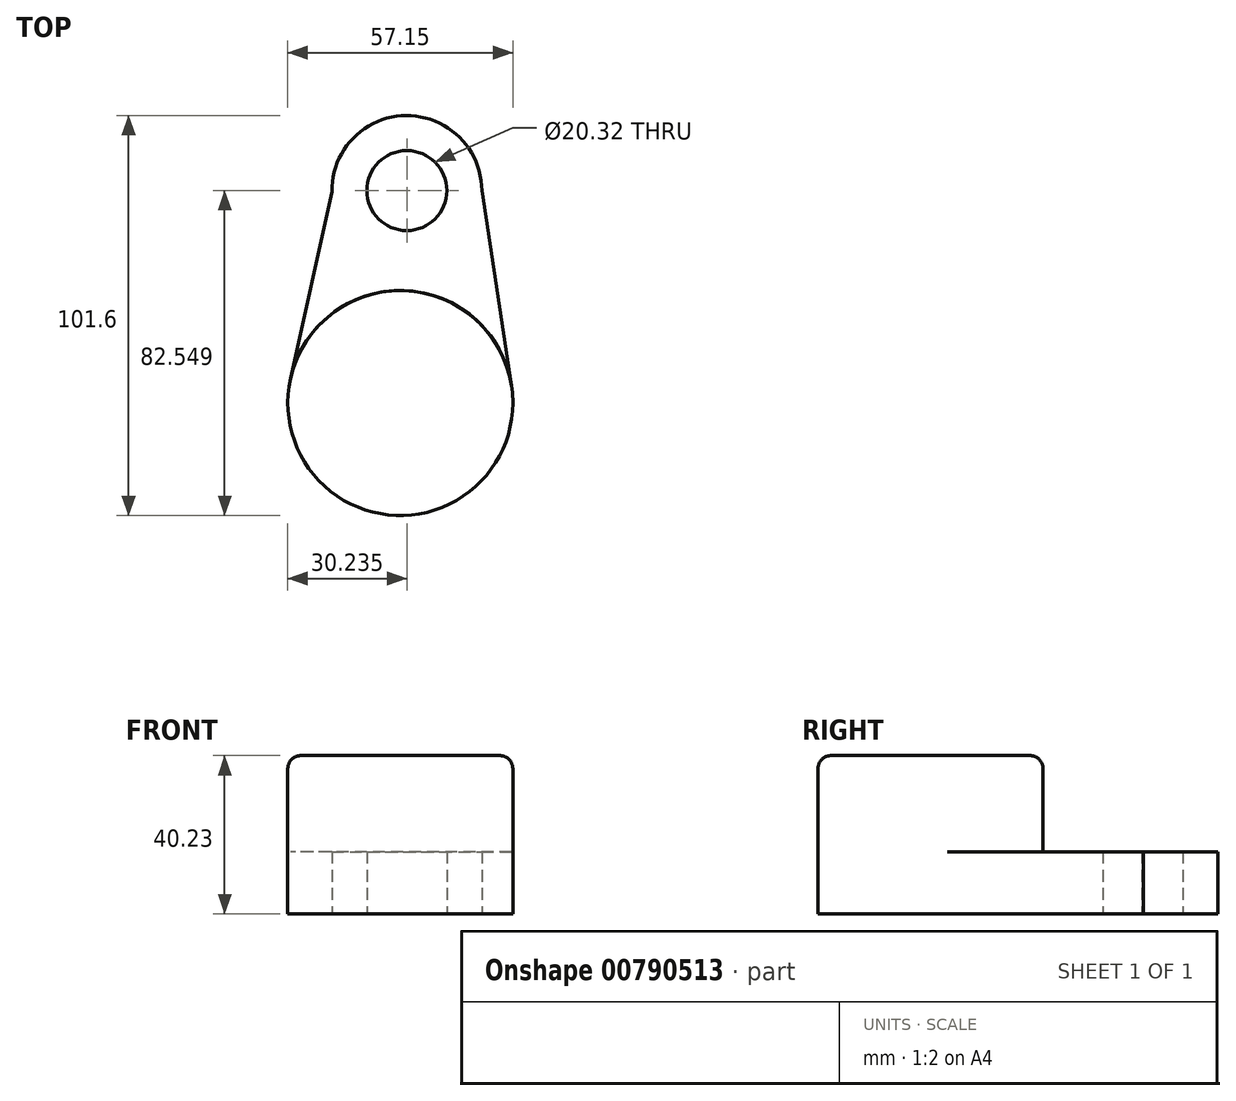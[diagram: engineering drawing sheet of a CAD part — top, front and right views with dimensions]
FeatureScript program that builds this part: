
annotation { "Feature Type Name" : "Feature", "Feature Type Description" : "" }
export const myFeature = defineFeature(function(context is Context, id is Id, definition is map)
    precondition{}
    {
        {
            var Q0;
            Q0=qCreatedBy(makeId("Top.planeOp"),FACE);
            var sketch = newSketch(context, id + "F0", { "sketchPlane" : qUnion([Q0])});
            skCircle(sketch, "E0", {"center": v(-37.45, -20.99) * mm, "radius": 28.58 * mm});
            skSolve(sketch);
        }
        {
            var Q0;
            Q0 = qSketchRegion(id + "F0", true);
            extrude(context, id + "F1", {"entities" : qUnion([Q0]), "depth" : 40.23 * mm, "offsetDistance" : 25.4 * mm});
        }
        {
            var Q0;
            Q0=makeQuery(id+"F1.opExtrude","CAP_FACE",FACE,{"disambiguationData":[OSD([sQuery(id+"F0.wireOp",EDGE,"E0")])],"isStart":false});
            fillet(context, id + "F2", {"entities" : qUnion([Q0]), "radius" : 3.3 * mm, "tangentPropagation" : true, "allowEdgeOverflow" : false});
        }
        {
            var Q0;
            Q0=makeQuery(id+"F1.opExtrude","CAP_FACE",FACE,{"disambiguationData":[OSD([sQuery(id+"F0.wireOp",EDGE,"E0")])],"isStart":false});
            var sketch = newSketch(context, id + "F3", { "sketchPlane" : qUnion([Q0])});
            skCircle(sketch, "E1", {"center": v(-37.45, -20.99) * mm, "radius": 10.67 * mm});
            skLineSegment(sketch, "E2.bottom", {"start": v(-33.61, -11.04) * mm, "end": v(-41.49, -11.04) * mm});
            skLineSegment(sketch, "E2.top", {"start": v(-33.61, -6.05) * mm, "end": v(-41.49, -6.05) * mm});
            skLineSegment(sketch, "E2.left", {"start": v(-33.61, -11.04) * mm, "end": v(-33.61, -6.05) * mm});
            skLineSegment(sketch, "E2.right", {"start": v(-41.49, -11.04) * mm, "end": v(-41.49, -6.05) * mm});
            skSolve(sketch);
        }
        {
            var Q0;
            Q0=makeQuery(id+"F1.opExtrude","CAP_FACE",FACE,{"disambiguationData":[OSD([sQuery(id+"F0.wireOp",EDGE,"E0")])],"isStart":true});
            var sketch = newSketch(context, id + "F4", { "sketchPlane" : qUnion([Q0])});
            skPoint(sketch, "E3.third.point", {"position": v(-36.17, -56.17) * mm});
            skCircle(sketch, "E4", {"center": v(-35.8, -32.99) * mm, "radius": 10.16 * mm});
            skArc(sketch, "E5", {"start": v(-54.84, -32.67) * mm, "mid": v(-35.98, -52.04) * mm, "end": v(-16.74, -33.04) * mm});
            skLineSegment(sketch, "E6", {"start": v(-54.84, -32.67) * mm, "end": v(-68.1, 27.2) * mm});
            skLineSegment(sketch, "E7", {"start": v(-16.74, -33.04) * mm, "end": v(-7.63, 27.06) * mm});
            skSolve(sketch);
        }
        {
            var Q0;
            Q0=makeQuery(id+"F4.imprint","IMPRINT",FACE,{"disambiguationData":[TD([[makeQuery(id+"F4.imprint","IMPRINT",EDGE,{"derivedFrom":sQuery(id+"F4.wireOp",EDGE,"E4")}),-1.0]])]});
            extrude(context, id + "F5", {"entities" : qUnion([Q0]), "operationType" : NewBodyOperationType.ADD, "oppositeDirection" : true, "depth" : 15.77 * mm, "offsetDistance" : 25.4 * mm});
        }
    });
